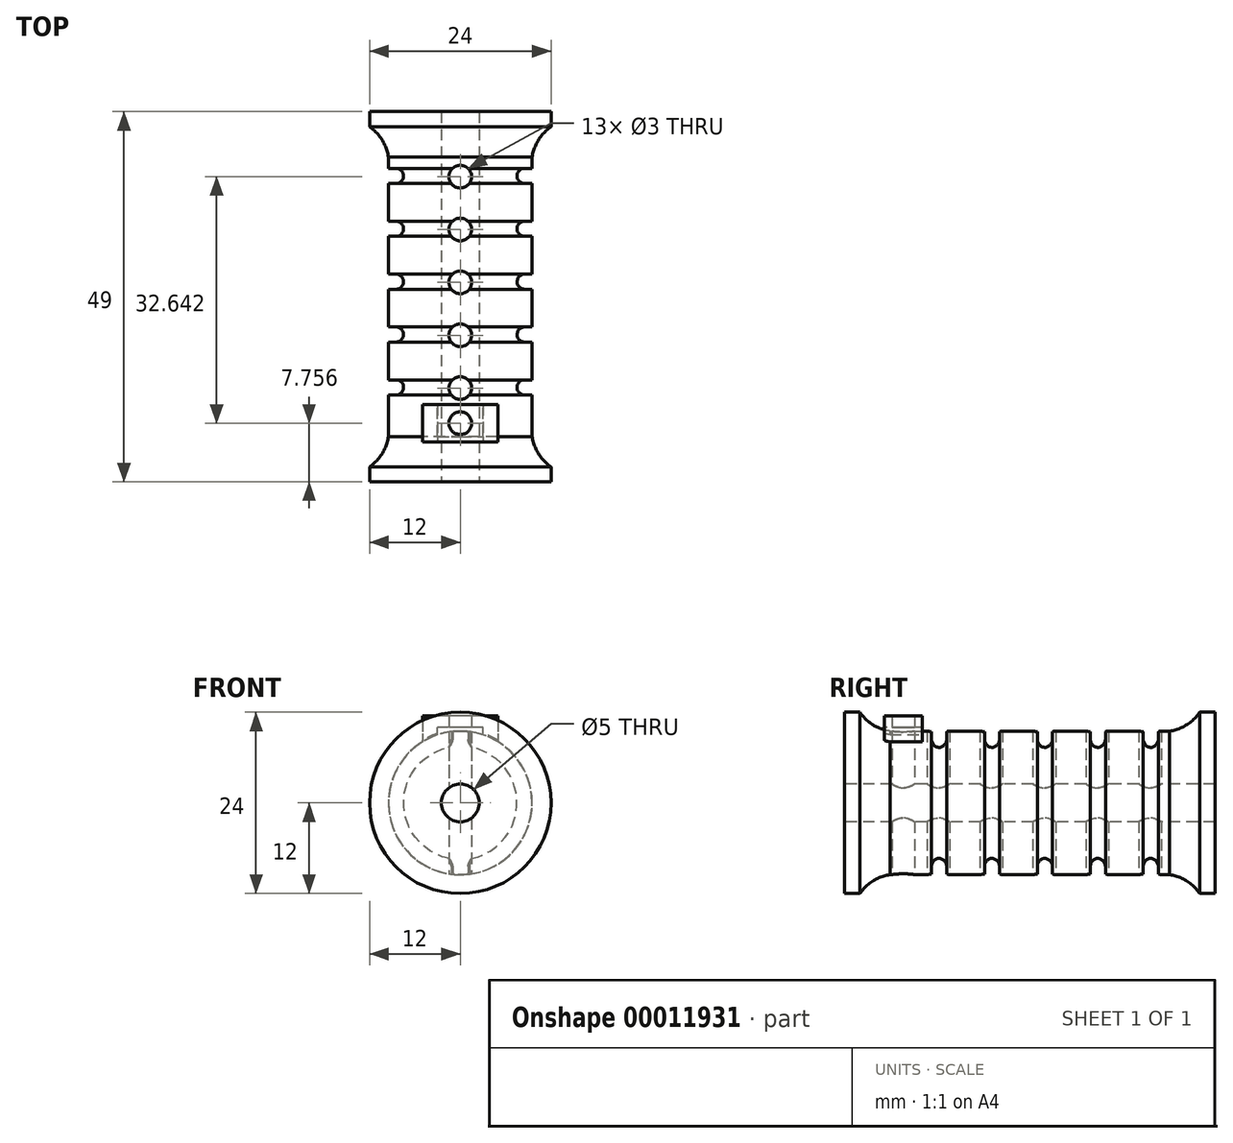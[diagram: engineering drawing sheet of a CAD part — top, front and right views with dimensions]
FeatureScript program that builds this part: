
annotation { "Feature Type Name" : "Feature", "Feature Type Description" : "" }
export const myFeature = defineFeature(function(context is Context, id is Id, definition is map)
    precondition{}
    {
        {
            var Q0;
            Q0=qCreatedBy(makeId("Front.planeOp"),FACE);
            var sketch = newSketch(context, id + "F0", { "sketchPlane" : qUnion([Q0])});
            skCircle(sketch, "E0", {"center": v(0, 0) * mm, "radius": 12 * mm});
            skSolve(sketch);
        }
        {
            var Q0;
            Q0=makeQuery(id+"F0.imprint","IMPRINT",FACE,{"disambiguationData":[TD([[makeQuery(id+"F0.imprint","IMPRINT",EDGE,{"derivedFrom":sQuery(id+"F0.wireOp",EDGE,"E0")}),1.0]])]});
            extrude(context, id + "F1", {"entities" : qUnion([Q0]), "depth" : 49 * mm});
        }
        {
            var Q0;
            Q0=makeQuery(id+"F1.opExtrude","CAP_FACE",FACE,{"disambiguationData":[OSD([sQuery(id+"F0.wireOp",EDGE,"E0")])],"isStart":false});
            var sketch = newSketch(context, id + "F2", { "sketchPlane" : qUnion([Q0])});
            skCircle(sketch, "E1", {"center": v(0, 0) * mm, "radius": 2.5 * mm});
            skSolve(sketch);
        }
        {
            var Q0;
            Q0 = qSketchRegion(id + "F2", true);
            extrude(context, id + "F3", {"entities" : qUnion([Q0]), "operationType" : NewBodyOperationType.REMOVE, "endBound" : BoundingType.THROUGH_ALL, "oppositeDirection" : true, "depth" : 25 * mm});
        }
        {
            var Q0;
            Q0=qCreatedBy(makeId("Right.planeOp"),FACE);
            var sketch = newSketch(context, id + "F4", { "sketchPlane" : qUnion([Q0])});
            skLineSegment(sketch, "E2.0", {"start": v(-49, -12) * mm, "end": v(-49, 12) * mm, "construction": true});
            skLineSegment(sketch, "E3", {"start": v(-49, 12) * mm, "end": v(-47, 12) * mm});
            skArc(sketch, "E4", {"start": v(-47, 12) * mm, "mid": v(-45.26, 10.34) * mm, "end": v(-43, 9.5) * mm});
            skLineSegment(sketch, "E5", {"start": v(-43, 9.5) * mm, "end": v(-24.5, 9.5) * mm});
            skLineSegment(sketch, "E6", {"start": v(-49, 0) * mm, "end": v(0, 0) * mm, "construction": true});
            skLineSegment(sketch, "E7", {"start": v(-24.5, 0) * mm, "end": v(-24.5, 12.6) * mm, "construction": true});
            skLineSegment(sketch, "E8", {"start": v(-49, 12) * mm, "end": v(-49, 17.12) * mm});
            skLineSegment(sketch, "E9", {"start": v(-49, 17.12) * mm, "end": v(-24.5, 17.12) * mm});
            skLineSegment(sketch, "E10.0.MirrorCS", {"start": v(0, -12) * mm, "end": v(0, 12) * mm, "construction": true});
            skLineSegment(sketch, "E10.1.MirrorCS", {"start": v(0, 12) * mm, "end": v(-2, 12) * mm});
            skArc(sketch, "E10.2.MirrorCS", {"start": v(-2, 12) * mm, "mid": v(-3.74, 10.34) * mm, "end": v(-6, 9.5) * mm});
            skLineSegment(sketch, "E10.3.MirrorCS", {"start": v(-6, 9.5) * mm, "end": v(-24.5, 9.5) * mm});
            skLineSegment(sketch, "E10.4.MirrorCS", {"start": v(0, 12) * mm, "end": v(0, 17.12) * mm});
            skLineSegment(sketch, "E10.5.MirrorCS", {"start": v(0, 17.12) * mm, "end": v(-24.5, 17.12) * mm});
            skSolve(sketch);
        }
        {
            var Q0;
            Q0=makeQuery(id+"F4.imprint","IMPRINT",FACE,{"disambiguationData":[TD([[makeQuery(id+"F4.imprint","IMPRINT",EDGE,{"derivedFrom":sQuery(id+"F4.wireOp",EDGE,"E3")}),1.0]])]});
            var Q1;
            Q1=sQuery(id+"F4.wireOp",EDGE,"E6");
            revolve(context, id + "F5", {"operationType" : NewBodyOperationType.REMOVE, "entities" : qUnion([Q0]), "axis" : qUnion([Q1]), "revolveType" : RevolveType.FULL, "oppositeDirection" : true});
        }
        {
            var Q0;
            Q0=qCreatedBy(makeId("Right.planeOp"),FACE);
            var sketch = newSketch(context, id + "F6", { "sketchPlane" : qUnion([Q0])});
            skLineSegment(sketch, "E11.0", {"start": v(-43, 9.5) * mm, "end": v(-43, -9.5) * mm, "construction": true});
            skArc(sketch, "E12", {"start": v(-37.5, 8.5) * mm, "mid": v(-36.5, 7.5) * mm, "end": v(-35.5, 8.5) * mm});
            skLineSegment(sketch, "E13", {"start": v(-36.5, 8.5) * mm, "end": v(-36.5, 7.5) * mm, "construction": true});
            skLineSegment(sketch, "E14", {"start": v(-37.5, 8.5) * mm, "end": v(-37.5, 10.03) * mm});
            skLineSegment(sketch, "E15", {"start": v(-37.5, 10.03) * mm, "end": v(-35.5, 10.03) * mm});
            skLineSegment(sketch, "E16", {"start": v(-35.5, 10.03) * mm, "end": v(-35.5, 8.5) * mm});
            skLineSegment(sketch, "E17.1.0.0", {"start": v(-30.5, 10.03) * mm, "end": v(-28.5, 10.03) * mm});
            skLineSegment(sketch, "E17.1.0.1", {"start": v(-30.5, 8.5) * mm, "end": v(-30.5, 10.03) * mm});
            skLineSegment(sketch, "E17.1.0.2", {"start": v(-29.5, 8.5) * mm, "end": v(-29.5, 7.5) * mm, "construction": true});
            skLineSegment(sketch, "E17.1.0.3", {"start": v(-28.5, 10.03) * mm, "end": v(-28.5, 8.5) * mm});
            skArc(sketch, "E17.1.0.4", {"start": v(-30.5, 8.5) * mm, "mid": v(-29.5, 7.5) * mm, "end": v(-28.5, 8.5) * mm});
            skLineSegment(sketch, "E17.2.0.0", {"start": v(-23.5, 10.03) * mm, "end": v(-21.5, 10.03) * mm});
            skLineSegment(sketch, "E17.2.0.1", {"start": v(-23.5, 8.5) * mm, "end": v(-23.5, 10.03) * mm});
            skLineSegment(sketch, "E17.2.0.2", {"start": v(-22.5, 8.5) * mm, "end": v(-22.5, 7.5) * mm, "construction": true});
            skLineSegment(sketch, "E17.2.0.3", {"start": v(-21.5, 10.03) * mm, "end": v(-21.5, 8.5) * mm});
            skArc(sketch, "E17.2.0.4", {"start": v(-23.5, 8.5) * mm, "mid": v(-22.5, 7.5) * mm, "end": v(-21.5, 8.5) * mm});
            skLineSegment(sketch, "E17.3.0.0", {"start": v(-16.5, 10.03) * mm, "end": v(-14.5, 10.03) * mm});
            skLineSegment(sketch, "E17.3.0.1", {"start": v(-16.5, 8.5) * mm, "end": v(-16.5, 10.03) * mm});
            skLineSegment(sketch, "E17.3.0.2", {"start": v(-15.5, 8.5) * mm, "end": v(-15.5, 7.5) * mm, "construction": true});
            skLineSegment(sketch, "E17.3.0.3", {"start": v(-14.5, 10.03) * mm, "end": v(-14.5, 8.5) * mm});
            skArc(sketch, "E17.3.0.4", {"start": v(-16.5, 8.5) * mm, "mid": v(-15.5, 7.5) * mm, "end": v(-14.5, 8.5) * mm});
            skLineSegment(sketch, "E17.4.0.0", {"start": v(-9.5, 10.03) * mm, "end": v(-7.5, 10.03) * mm});
            skLineSegment(sketch, "E17.4.0.1", {"start": v(-9.5, 8.5) * mm, "end": v(-9.5, 10.03) * mm});
            skLineSegment(sketch, "E17.4.0.2", {"start": v(-8.5, 8.5) * mm, "end": v(-8.5, 7.5) * mm, "construction": true});
            skLineSegment(sketch, "E17.4.0.3", {"start": v(-7.5, 10.03) * mm, "end": v(-7.5, 8.5) * mm});
            skArc(sketch, "E17.4.0.4", {"start": v(-9.5, 8.5) * mm, "mid": v(-8.5, 7.5) * mm, "end": v(-7.5, 8.5) * mm});
            skLineSegment(sketch, "E17.direction1", {"start": v(-37.5, 10.03) * mm, "end": v(-30.5, 10.03) * mm, "construction": true});
            skLineSegment(sketch, "E18", {"start": v(-43, 0) * mm, "end": v(0, 0) * mm, "construction": true});
            skSolve(sketch);
        }
        {
            var Q0;
            Q0 = qSketchRegion(id + "F6", true);
            var Q1;
            Q1=sQuery(id+"F6.wireOp",EDGE,"E18");
            revolve(context, id + "F7", {"operationType" : NewBodyOperationType.REMOVE, "entities" : qUnion([Q0]), "axis" : qUnion([Q1]), "revolveType" : RevolveType.FULL, "oppositeDirection" : true});
        }
        {
            var Q0;
            Q0=qCreatedBy(makeId("Top.planeOp"),FACE);
            cPlane(context, id + "F8", {"entities" : qUnion([Q0]), "cplaneType" : CPlaneType.OFFSET, "offset" : 12 * mm, "oppositeDirection" : true, "width" : 150 * mm, "height" : 150 * mm});
        }
        {
            var Q0;
            Q0=qCreatedBy(id+"F8.planeOp",FACE);
            var sketch = newSketch(context, id + "F9", { "sketchPlane" : qUnion([Q0])});
            skCircle(sketch, "E19", {"center": v(0, -8.6) * mm, "radius": 1.5 * mm});
            skCircle(sketch, "E20", {"center": v(0, -15.6) * mm, "radius": 1.5 * mm});
            skLineSegment(sketch, "E21", {"start": v(0, 0) * mm, "end": v(0, -51.8) * mm, "construction": true});
            skCircle(sketch, "E22.0.1.0", {"center": v(0, -22.6) * mm, "radius": 1.5 * mm});
            skCircle(sketch, "E22.0.2.0", {"center": v(0, -29.6) * mm, "radius": 1.5 * mm});
            skCircle(sketch, "E22.0.3.0", {"center": v(0, -36.6) * mm, "radius": 1.5 * mm});
            skLineSegment(sketch, "E22.direction1", {"start": v(0, -15.6) * mm, "end": v(25, -15.6) * mm, "construction": true});
            skLineSegment(sketch, "E22.direction2", {"start": v(0, -15.6) * mm, "end": v(0, -22.6) * mm, "construction": true});
            skCircle(sketch, "E23", {"center": v(0, -41.24) * mm, "radius": 1.5 * mm});
            skSolve(sketch);
        }
        {
            var Q0;
            Q0 = qSketchRegion(id + "F9", true);
            extrude(context, id + "F10", {"entities" : qUnion([Q0]), "operationType" : NewBodyOperationType.REMOVE, "depth" : 25 * mm});
        }
        {
            var Q0;
            Q0=qCreatedBy(makeId("Top.planeOp"),FACE);
            cPlane(context, id + "F11", {"entities" : qUnion([Q0]), "cplaneType" : CPlaneType.OFFSET, "offset" : 10 * mm, "width" : 150 * mm, "height" : 150 * mm});
        }
        {
            var Q0;
            Q0=qCreatedBy(id+"F11.planeOp",FACE);
            var sketch = newSketch(context, id + "F12", { "sketchPlane" : qUnion([Q0])});
            skCircle(sketch, "E24.0", {"center": v(0, -41.24) * mm, "radius": 1.5 * mm});
            skLineSegment(sketch, "E25.bottom", {"start": v(5, -38.74) * mm, "end": v(-5, -38.74) * mm});
            skLineSegment(sketch, "E25.top", {"start": v(5, -43.74) * mm, "end": v(-5, -43.74) * mm});
            skLineSegment(sketch, "E25.left", {"start": v(5, -38.74) * mm, "end": v(5, -43.74) * mm});
            skLineSegment(sketch, "E25.right", {"start": v(-5, -38.74) * mm, "end": v(-5, -43.74) * mm});
            skPoint(sketch, "E26", {"position": v(5, -41.24) * mm});
            skSolve(sketch);
        }
        {
            var Q0;
            Q0=makeQuery(id+"F12.imprint","IMPRINT",FACE,{"disambiguationData":[TD([[makeQuery(id+"F12.imprint","IMPRINT",EDGE,{"derivedFrom":sQuery(id+"F12.wireOp",EDGE,"E24.0")}),-1.0]])]});
            extrude(context, id + "F13", {"entities" : qUnion([Q0]), "depth" : 1.5 * mm});
        }
        {
            var Q0;
            Q0=makeQuery(id+"F13.opExtrude","CAP_FACE",FACE,{"disambiguationData":[OSD([sQuery(id+"F12.wireOp",EDGE,"E24.0"),sQuery(id+"F12.wireOp",EDGE,"E25.bottom"),sQuery(id+"F12.wireOp",EDGE,"E25.top"),sQuery(id+"F12.wireOp",EDGE,"E25.left"),sQuery(id+"F12.wireOp",EDGE,"E25.right")])],"isStart":true});
            var sketch = newSketch(context, id + "F14", { "sketchPlane" : qUnion([Q0])});
            skLineSegment(sketch, "E27.bottom", {"start": v(-5, 38.74) * mm, "end": v(-3, 38.74) * mm});
            skLineSegment(sketch, "E27.top", {"start": v(-5, 43.74) * mm, "end": v(-3, 43.74) * mm});
            skLineSegment(sketch, "E27.left", {"start": v(-5, 38.74) * mm, "end": v(-5, 43.74) * mm});
            skLineSegment(sketch, "E27.right", {"start": v(-3, 38.74) * mm, "end": v(-3, 43.74) * mm});
            skLineSegment(sketch, "E28", {"start": v(0, 41.24) * mm, "end": v(0, 36.83) * mm, "construction": true});
            skLineSegment(sketch, "E29.0.MirrorCS", {"start": v(5, 38.74) * mm, "end": v(5, 43.74) * mm});
            skLineSegment(sketch, "E29.1.MirrorCS", {"start": v(3, 38.74) * mm, "end": v(3, 43.74) * mm});
            skLineSegment(sketch, "E29.2.MirrorCS", {"start": v(5, 43.74) * mm, "end": v(3, 43.74) * mm});
            skLineSegment(sketch, "E29.3.MirrorCS", {"start": v(5, 38.74) * mm, "end": v(3, 38.74) * mm});
            skSolve(sketch);
        }
        {
            var Q0;
            Q0 = qSketchRegion(id + "F14", true);
            extrude(context, id + "F15", {"entities" : qUnion([Q0]), "operationType" : NewBodyOperationType.ADD, "endBound" : BoundingType.UP_TO_NEXT, "depth" : 25 * mm});
        }
    });
